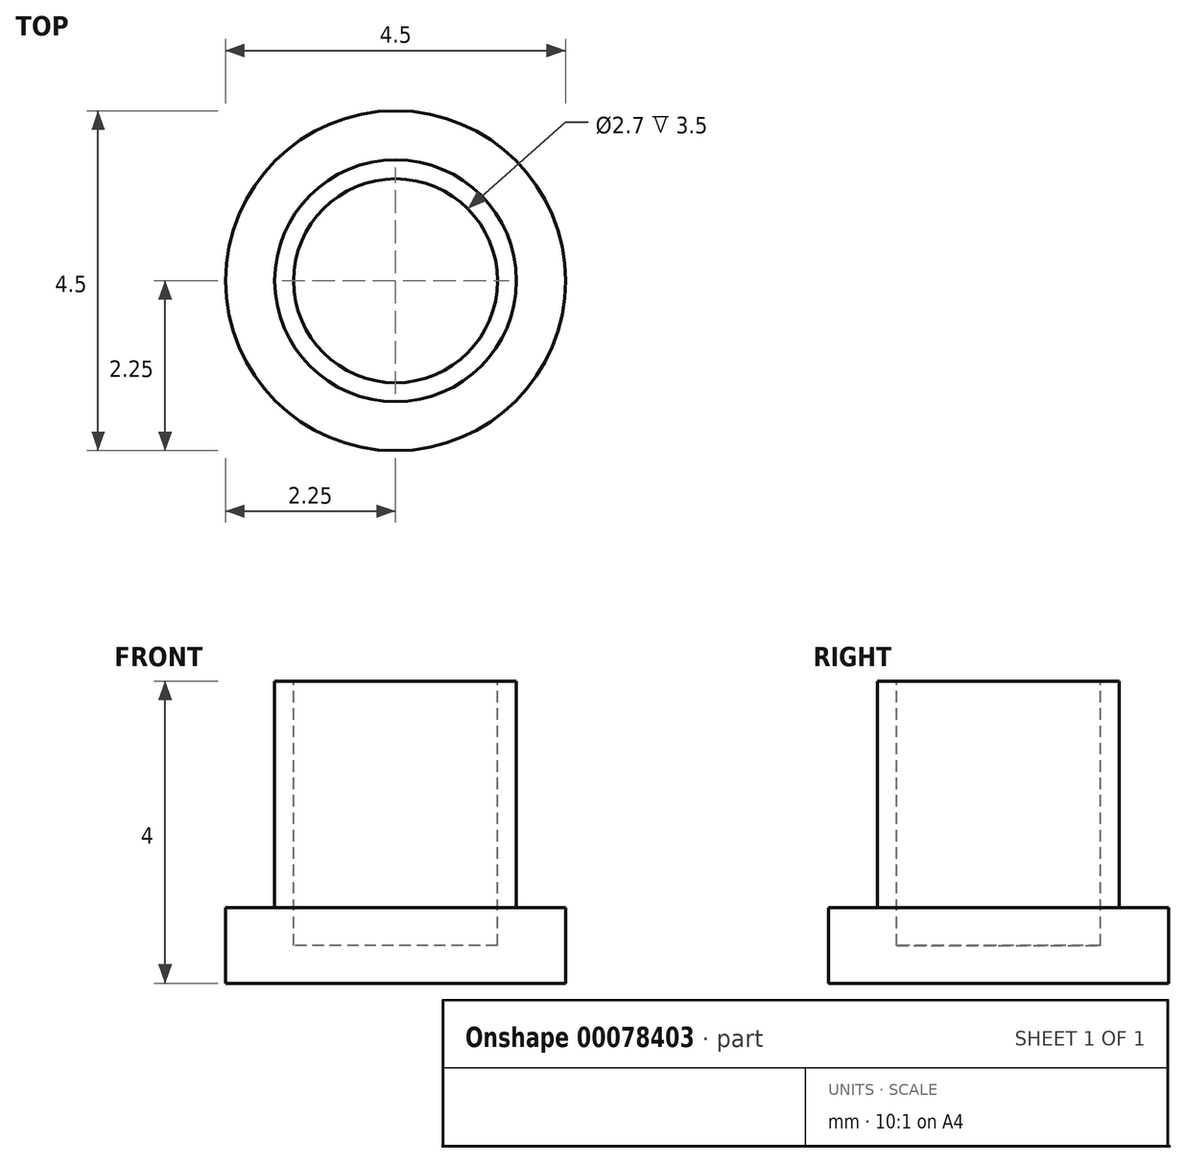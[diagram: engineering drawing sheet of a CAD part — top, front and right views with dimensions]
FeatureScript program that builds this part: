
annotation { "Feature Type Name" : "Feature", "Feature Type Description" : "" }
export const myFeature = defineFeature(function(context is Context, id is Id, definition is map)
    precondition{}
    {
        {
            var Q0;
            Q0=qCreatedBy(makeId("Top.planeOp"),FACE);
            var sketch = newSketch(context, id + "F0", { "sketchPlane" : qUnion([Q0])});
            skCircle(sketch, "E0", {"center": v(0, 0) * mm, "radius": 2.25 * mm});
            skSolve(sketch);
        }
        {
            var Q0;
            Q0=makeQuery(id+"F0.imprint","IMPRINT",FACE,{"disambiguationData":[TD([[makeQuery(id+"F0.imprint","IMPRINT",EDGE,{"derivedFrom":sQuery(id+"F0.wireOp",EDGE,"E0")}),1.0]])]});
            extrude(context, id + "F1", {"entities" : qUnion([Q0]), "depth" : 1 * mm, "offsetDistance" : 25 * mm});
        }
        {
            var Q0;
            Q0=makeQuery(id+"F1.opExtrude","CAP_FACE",FACE,{"disambiguationData":[OSD([sQuery(id+"F0.wireOp",EDGE,"E0")])],"isStart":false});
            var sketch = newSketch(context, id + "F2", { "sketchPlane" : qUnion([Q0])});
            skCircle(sketch, "E1", {"center": v(0, 0) * mm, "radius": 1.6 * mm});
            skSolve(sketch);
        }
        {
            var Q0;
            Q0 = qSketchRegion(id + "F2", true);
            extrude(context, id + "F3", {"entities" : qUnion([Q0]), "operationType" : NewBodyOperationType.ADD, "depth" : 3 * mm, "offsetDistance" : 25 * mm});
        }
        {
            var Q0;
            Q0=makeQuery(id+"F3.opExtrude","CAP_FACE",FACE,{"disambiguationData":[OSD([sQuery(id+"F2.wireOp",EDGE,"E1")])],"isStart":false});
            var sketch = newSketch(context, id + "F4", { "sketchPlane" : qUnion([Q0])});
            skCircle(sketch, "E2", {"center": v(0, 0) * mm, "radius": 1.35 * mm});
            skSolve(sketch);
        }
        {
            var Q0;
            Q0=makeQuery(id+"F4.imprint","IMPRINT",FACE,{"disambiguationData":[TD([[makeQuery(id+"F4.imprint","IMPRINT",EDGE,{"derivedFrom":sQuery(id+"F4.wireOp",EDGE,"E2")}),1.0]])]});
            extrude(context, id + "F5", {"entities" : qUnion([Q0]), "operationType" : NewBodyOperationType.REMOVE, "oppositeDirection" : true, "depth" : 3.5 * mm, "offsetDistance" : 25 * mm});
        }
    });
